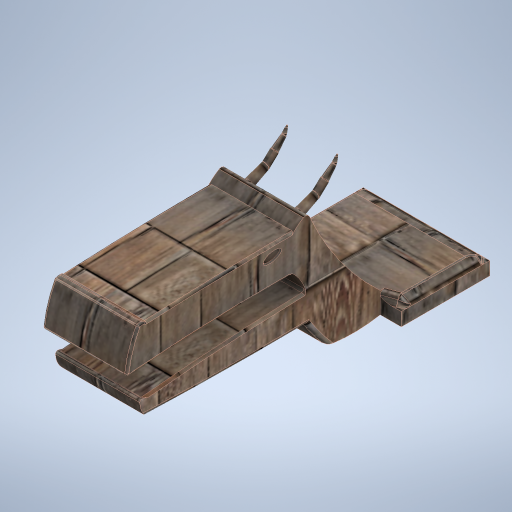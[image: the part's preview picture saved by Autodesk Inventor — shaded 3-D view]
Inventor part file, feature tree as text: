
AUTODESK INVENTOR PART (.ipt)
format: ipt  version: 2024.2 (Build 282272000, 272)  size: 1,789,952 bytes
history: native  units: mm
features: sketch x28, extrude x18, fillet x18, plane x4, chamfer x2, draft x1
ambient origin geometry x8: Origin, YZ Plane, XZ Plane, XY Plane, X Axis, Y Axis, Z Axis, Center Point
bodies: Solid1 (feature_tree)
feature tree (71):
  sketch  "Sketch1"  dims[d0=300.0mm d1=210.0mm]
  sketch  "Sketch2"  dims[d2=300.0mm d3=6.108652mm d4=700.0mm d5=350.0mm]
  sketch  "Sketch3"  dims[d6=7000.0mm]
  extrude  "Extrusion1"  Depth=210.0mm
  extrude  "Extrusion2"  Depth=6.108652mm
  fillet  "Fillet1"  Radius=700.0mm
  fillet  "Fillet2"  Radius=350.0mm
  plane  "Work Plane1"
  chamfer  "Chamfer1"  Distance=50.0mm
  fillet  "Fillet3"  Radius=200.0mm
  chamfer  "Chamfer2"  Distance=18.5mm Angle=45.0deg
  fillet  "Fillet4"  Radius=80.0mm
  fillet  "Fillet5"  Radius=80.0mm
  extrude  "Extrusion3"  Depth=31.5mm TaperAngle=0.0deg
  sketch  "Sketch5"  dims[d8=250.0mm]
  extrude  "Extrusion4"  Depth=5.0mm
  fillet  "Fillet6"  Radius=5.0mm
  fillet  "Fillet7"  Radius=5.0mm
  fillet  "Fillet8"  [1 undecoded]
  extrude  "Extrusion5"  Depth=2.5mm
  extrude  "Extrusion6"  Depth=2.5mm
  fillet  "Fillet9"  Radius=150.0mm
  fillet  "Fillet10"  Radius=31.5mm
  fillet  "Fillet11"  Radius=1000.0mm
  sketch  "Sketch9"  dims[d12=60.0mm]
  extrude  "Extrusion7"  Depth=9.5mm
  extrude  "Extrusion8"  Depth=40.0mm TaperAngle=0.0deg
  extrude  "Extrusion9"  Depth=0.436332mm
  extrude  "Extrusion10"  Depth=3.4mm TaperAngle=0.0deg
  fillet  "Fillet12"  Radius=0.25mm
  plane  "Work Plane2"
  extrude  "Extrusion11"  Depth=30.0mm TaperAngle=0.0deg
  sketch  "Sketch15"  dims[d18=350.0mm]
  extrude  "Extrusion12"  Depth=2.0mm
  fillet  "Fillet13"  Radius=30.0mm
  sketch  "Sketch17"  dims[d20=60.0mm d21=50.0mm d22=0.0mm d23=200.0mm d24=0.0mm]
  draft  "FaceDraft1"
  sketch  "Sketch18"  dims[d25=5.0mm]
  plane  "Work Plane3"
  extrude  "Extrusion13"  Depth=2.0mm
  fillet  "Fillet14"  Radius=3.490659mm
  extrude  "Extrusion14"  Depth=5.0mm TaperAngle=0.0deg
  fillet  "Fillet15"  Radius=2.0mm
  extrude  "Extrusion15"  Depth=10.0mm
  fillet  "Fillet16"  Radius=5.0mm
  sketch  "Sketch22"  dims[d38=31.5mm d39=31.5mm d40=-0.872665mm d41=-0.872665mm d42=5.0mm d43=5.0mm d44=5.0mm d45=0.0mm d46=0.0mm]
  sketch  "Sketch23"  dims[d47=150.0mm d48=0.0mm d49=2.5mm]
  sketch  "Sketch24"  dims[d50=2.5mm d51=2.5mm d52=150.0mm d53=0.0mm d54=31.5mm d55=0.0mm d56=1000.0mm d57=0.0mm]
  plane  "Work Plane4"
  extrude  "Extrusion16"  Depth=0.99mm
  fillet  "Fillet17"  [1 undecoded]
  extrude  "Extrusion17"  TaperAngle=0.0deg  [1 undecoded]
  sketch  "Sketch27"  dims[d65=5.25mm d66=0.436332mm]
  extrude  "Extrusion18"  TaperAngle=0.0deg  [1 undecoded]
  fillet  "Fillet18"  [1 undecoded]
  sketch  "Sketch4"  dims[d7=25.0mm]
  sketch  "Sketch6"  dims[d9=40.0mm]
  sketch  "Sketch7"  dims[d10=15.358897mm]
  sketch  "Sketch8"  dims[d11=4000.0mm]
  sketch  "Sketch10"  dims[d13=125.0mm]
  sketch  "Sketch11"  dims[d14=5000.0mm]
  sketch  "Sketch12"  dims[d15=50.0mm]
  sketch  "Sketch13"  dims[d16=6200.0mm]
  sketch  "Sketch14"  dims[d17=625.0mm]
  sketch  "Sketch16"  dims[d19=49.866924mm]
  sketch  "Sketch19"  dims[d26=10.0mm d27=18.5mm d28=125.0mm d29=45.0deg d30=80.0mm]
  sketch  "Sketch20"  dims[d31=18.5mm d32=125.0mm d33=45.0deg d34=80.0mm]
  sketch  "Sketch21"  dims[d35=50.0mm d36=31.5mm d37=0.0mm]
  sketch  "Sketch25"  dims[d58=31.5mm d59=0.0mm d60=9.5mm]
  sketch  "Sketch26"  dims[d61=10.0mm d62=0.0mm d63=40.0mm d64=0.0mm]
  sketch  "Sketch28"  dims[d67=-3.490659mm d68=3.4mm d69=0.0mm d70=0.25mm d71=30.0mm d72=0.0mm d73=2.0mm d74=30.0mm d75=-0.872665mm d76=2.0mm d77=3.490659mm d78=5.0mm d79=3.0mm d80=0.0mm d81=0.0mm d82=2.0mm d83=10.0mm d84=-1.745329mm d85=5.0mm d86=-1.745329mm d87=0.99mm d88=0.0mm d89=0.0mm d90=0.0mm]
note: 5 required parameter values undecoded (feature->parameter linkage not recoverable at this tier; creation-order binding heuristic only, values carry confidence <= 0.55)
